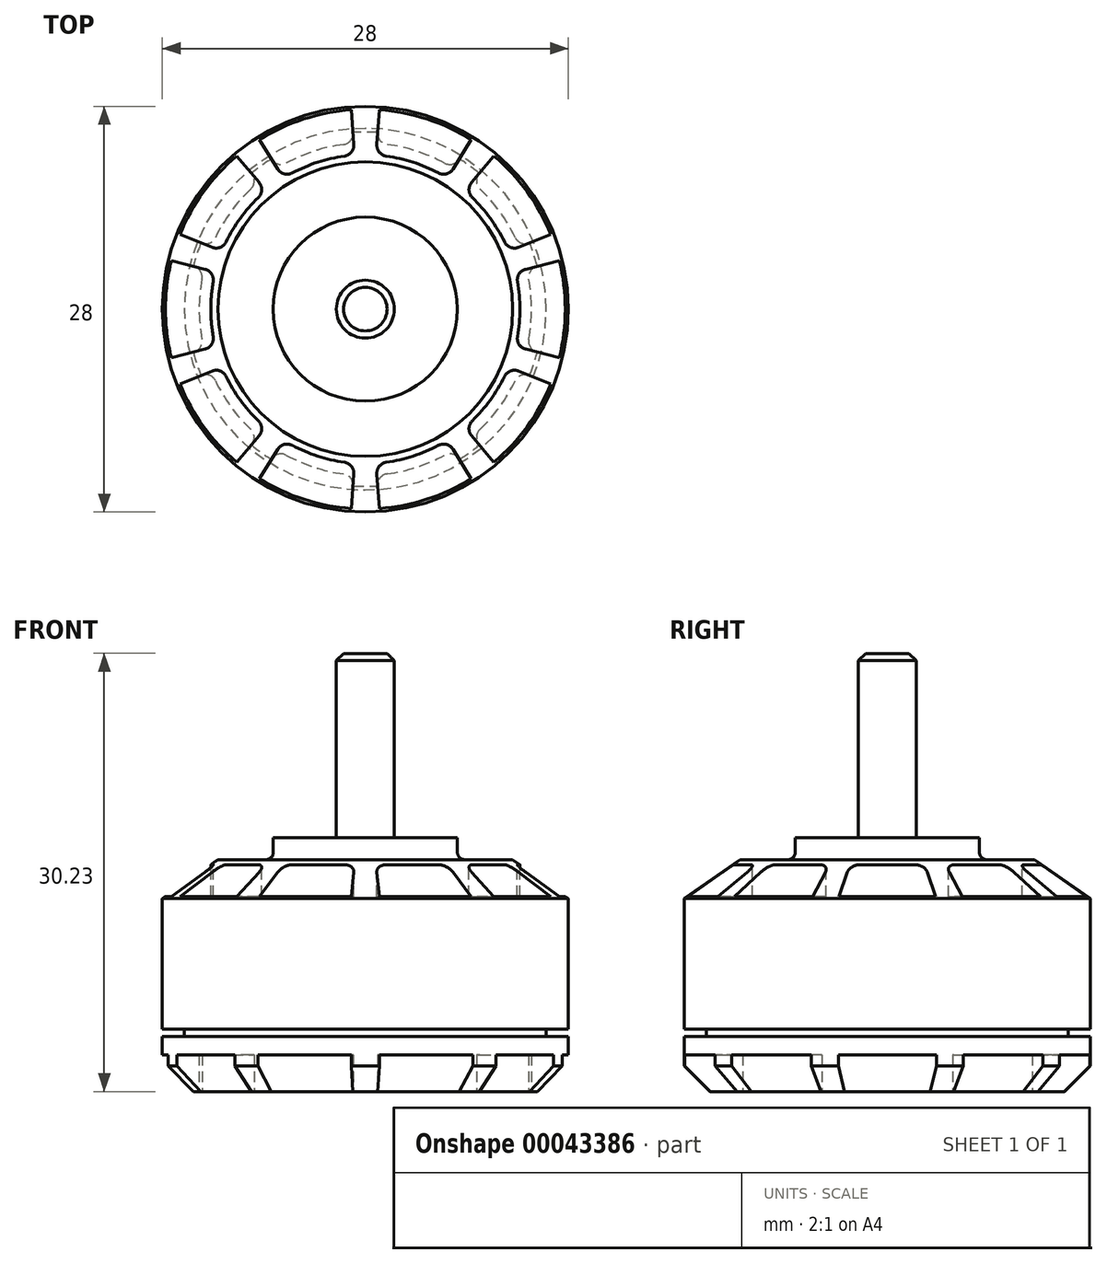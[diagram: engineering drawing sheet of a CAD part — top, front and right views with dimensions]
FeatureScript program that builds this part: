
annotation { "Feature Type Name" : "Feature", "Feature Type Description" : "" }
export const myFeature = defineFeature(function(context is Context, id is Id, definition is map)
    precondition{}
    {
        {
            var Q0;
            Q0=qCreatedBy(makeId("Front.planeOp"),FACE);
            var sketch = newSketch(context, id + "F0", { "sketchPlane" : qUnion([Q0])});
            skLineSegment(sketch, "E0", {"start": v(0, 0) * mm, "end": v(0, 46.88) * mm, "construction": true});
            skLineSegment(sketch, "E1", {"start": v(0, 0) * mm, "end": v(12.22, 0) * mm});
            skLineSegment(sketch, "E2", {"start": v(12.22, 0) * mm, "end": v(14, 1.78) * mm});
            skLineSegment(sketch, "E3", {"start": v(14, 1.78) * mm, "end": v(14, 3.81) * mm});
            skLineSegment(sketch, "E4", {"start": v(14, 3.81) * mm, "end": v(12.48, 3.81) * mm});
            skLineSegment(sketch, "E5", {"start": v(12.48, 3.81) * mm, "end": v(12.48, 4.31) * mm});
            skLineSegment(sketch, "E6", {"start": v(12.48, 4.3) * mm, "end": v(14, 4.31) * mm});
            skLineSegment(sketch, "E7", {"start": v(14, 4.31) * mm, "end": v(14, 13.31) * mm});
            skLineSegment(sketch, "E8", {"start": v(14, 13.31) * mm, "end": v(10.16, 16) * mm});
            skLineSegment(sketch, "E9", {"start": v(10.16, 16) * mm, "end": v(6.35, 16) * mm});
            skLineSegment(sketch, "E10", {"start": v(6.35, 16) * mm, "end": v(6.35, 17.53) * mm});
            skLineSegment(sketch, "E11", {"start": v(6.35, 17.53) * mm, "end": v(2, 17.53) * mm});
            skLineSegment(sketch, "E12", {"start": v(2, 17.53) * mm, "end": v(2, 30.23) * mm});
            skLineSegment(sketch, "E13", {"start": v(2, 30.23) * mm, "end": v(0, 30.23) * mm});
            skLineSegment(sketch, "E14", {"start": v(0, 30.23) * mm, "end": v(0, 0) * mm});
            skSolve(sketch);
        }
        {
            var Q0;
            Q0 = qSketchRegion(id + "F0", true);
            var Q1;
            Q1=sQuery(id+"F0.wireOp",EDGE,"E0");
            revolve(context, id + "F1", {"entities" : qUnion([Q0]), "axis" : qUnion([Q1]), "revolveType" : RevolveType.FULL});
        }
        {
            var Q0;
            Q0=makeQuery(id+"F1.opRevolve","SWEPT_EDGE",EDGE,{"disambiguationData":[OSD([sQuery(id+"F0.wireOp",EDGE,"E12"),sQuery(id+"F0.wireOp",EDGE,"E13")])]});
            chamfer(context, id + "F2", {"entities" : qUnion([Q0]), "width" : .5 * mm, "tangentPropagation" : true});
        }
        {
            var Q0;
            Q0=makeQuery(id+"F1.opRevolve","SWEPT_EDGE",EDGE,{"disambiguationData":[OSD([sQuery(id+"F0.wireOp",EDGE,"E9"),sQuery(id+"F0.wireOp",EDGE,"E10")])]});
            fillet(context, id + "F3", {"entities" : qUnion([Q0]), "radius" : .5 * mm, "tangentPropagation" : true, "allowEdgeOverflow" : false});
        }
        {
            var Q0;
            Q0=makeQuery(id+"F1.opRevolve","SWEPT_FACE",FACE,{"disambiguationData":[OSD([sQuery(id+"F0.wireOp",EDGE,"E9")])]});
            var sketch = newSketch(context, id + "F4", { "sketchPlane" : qUnion([Q0])});
            skArc(sketch, "E15.0", {"start": v(10.5, 1.88) * mm, "mid": v(10.62, 0.95) * mm, "end": v(10.66, 0) * mm});
            skLineSegment(sketch, "E16", {"start": v(11.06, 2.76) * mm, "end": v(13.58, 3.39) * mm});
            skLineSegment(sketch, "E17", {"start": v(0, 0) * mm, "end": v(17.06, 0) * mm, "construction": true});
            skPoint(sketch, "E18.visualSharp", {"position": v(10.34, 2.58) * mm});
            skArc(sketch, "E18.filletArc", {"start": v(11.06, 2.76) * mm, "mid": v(10.6, 2.43) * mm, "end": v(10.5, 1.88) * mm});
            skArc(sketch, "E19.MirrorCS", {"start": v(10.5, -1.88) * mm, "mid": v(10.62, -0.95) * mm, "end": v(10.66, 0) * mm});
            skArc(sketch, "E20.MirrorCS", {"start": v(11.06, -2.76) * mm, "mid": v(10.6, -2.43) * mm, "end": v(10.5, -1.88) * mm});
            skLineSegment(sketch, "E21.MirrorCS", {"start": v(11.06, -2.76) * mm, "end": v(13.58, -3.39) * mm});
            skArc(sketch, "E22.1", {"start": v(13.58, -3.39) * mm, "mid": v(14, 0) * mm, "end": v(13.58, 3.39) * mm});
            skLineSegment(sketch, "E23.1.0", {"start": v(7.33, 8.73) * mm, "end": v(9, 10.72) * mm});
            skArc(sketch, "E23.1.1", {"start": v(7.33, 8.73) * mm, "mid": v(7.15, 8.2) * mm, "end": v(7.38, 7.7) * mm});
            skArc(sketch, "E23.1.2", {"start": v(9.6, 4.64) * mm, "mid": v(9.15, 5.48) * mm, "end": v(8.62, 6.27) * mm});
            skArc(sketch, "E23.1.3", {"start": v(10.57, 4.27) * mm, "mid": v(10, 4.26) * mm, "end": v(9.6, 4.64) * mm});
            skLineSegment(sketch, "E23.1.4", {"start": v(10.57, 4.27) * mm, "end": v(12.98, 5.24) * mm});
            skArc(sketch, "E23.1.5", {"start": v(12.98, 5.24) * mm, "mid": v(11.33, 8.23) * mm, "end": v(9, 10.72) * mm});
            skArc(sketch, "E23.1.6", {"start": v(7.38, 7.7) * mm, "mid": v(8.03, 7) * mm, "end": v(8.62, 6.27) * mm});
            skPoint(sketch, "E23.1.7", {"position": v(6.85, 8.17) * mm});
            skLineSegment(sketch, "E23.2.0", {"start": v(0.8, 11.37) * mm, "end": v(0.98, 13.97) * mm});
            skArc(sketch, "E23.2.1", {"start": v(0.8, 11.37) * mm, "mid": v(0.96, 10.84) * mm, "end": v(1.45, 10.56) * mm});
            skArc(sketch, "E23.2.2", {"start": v(5.03, 9.4) * mm, "mid": v(4.18, 9.8) * mm, "end": v(3.3, 10.14) * mm});
            skArc(sketch, "E23.2.3", {"start": v(6.04, 9.66) * mm, "mid": v(5.59, 9.33) * mm, "end": v(5.03, 9.4) * mm});
            skLineSegment(sketch, "E23.2.4", {"start": v(6.04, 9.66) * mm, "end": v(7.42, 11.87) * mm});
            skArc(sketch, "E23.2.5", {"start": v(7.42, 11.87) * mm, "mid": v(4.33, 13.31) * mm, "end": v(0.98, 13.97) * mm});
            skArc(sketch, "E23.2.6", {"start": v(1.45, 10.56) * mm, "mid": v(2.38, 10.4) * mm, "end": v(3.3, 10.14) * mm});
            skPoint(sketch, "E23.2.7", {"position": v(0.74, 10.63) * mm});
            skLineSegment(sketch, "E23.3.0", {"start": v(-6.04, 9.66) * mm, "end": v(-7.42, 11.87) * mm});
            skArc(sketch, "E23.3.1", {"start": v(-6.04, 9.66) * mm, "mid": v(-5.59, 9.33) * mm, "end": v(-5.03, 9.4) * mm});
            skArc(sketch, "E23.3.2", {"start": v(-1.45, 10.56) * mm, "mid": v(-2.38, 10.4) * mm, "end": v(-3.3, 10.14) * mm});
            skArc(sketch, "E23.3.3", {"start": v(-0.8, 11.37) * mm, "mid": v(-0.96, 10.84) * mm, "end": v(-1.45, 10.56) * mm});
            skLineSegment(sketch, "E23.3.4", {"start": v(-0.8, 11.37) * mm, "end": v(-0.98, 13.97) * mm});
            skArc(sketch, "E23.3.5", {"start": v(-0.98, 13.97) * mm, "mid": v(-4.33, 13.31) * mm, "end": v(-7.42, 11.87) * mm});
            skArc(sketch, "E23.3.6", {"start": v(-5.03, 9.4) * mm, "mid": v(-4.18, 9.8) * mm, "end": v(-3.3, 10.14) * mm});
            skPoint(sketch, "E23.3.7", {"position": v(-5.65, 9.04) * mm});
            skLineSegment(sketch, "E23.4.0", {"start": v(-10.57, 4.27) * mm, "end": v(-12.98, 5.24) * mm});
            skArc(sketch, "E23.4.1", {"start": v(-10.57, 4.27) * mm, "mid": v(-10, 4.26) * mm, "end": v(-9.6, 4.64) * mm});
            skArc(sketch, "E23.4.2", {"start": v(-7.38, 7.7) * mm, "mid": v(-8.03, 7) * mm, "end": v(-8.62, 6.27) * mm});
            skArc(sketch, "E23.4.3", {"start": v(-7.33, 8.73) * mm, "mid": v(-7.15, 8.2) * mm, "end": v(-7.38, 7.7) * mm});
            skLineSegment(sketch, "E23.4.4", {"start": v(-7.33, 8.73) * mm, "end": v(-9, 10.72) * mm});
            skArc(sketch, "E23.4.5", {"start": v(-9, 10.72) * mm, "mid": v(-11.33, 8.23) * mm, "end": v(-12.98, 5.24) * mm});
            skArc(sketch, "E23.4.6", {"start": v(-9.6, 4.64) * mm, "mid": v(-9.15, 5.48) * mm, "end": v(-8.62, 6.27) * mm});
            skPoint(sketch, "E23.4.7", {"position": v(-9.88, 4) * mm});
            skLineSegment(sketch, "E23.5.0", {"start": v(-11.06, -2.76) * mm, "end": v(-13.58, -3.39) * mm});
            skArc(sketch, "E23.5.1", {"start": v(-11.06, -2.76) * mm, "mid": v(-10.6, -2.43) * mm, "end": v(-10.5, -1.88) * mm});
            skArc(sketch, "E23.5.2", {"start": v(-10.5, 1.88) * mm, "mid": v(-10.62, 0.95) * mm, "end": v(-10.66, 0) * mm});
            skArc(sketch, "E23.5.3", {"start": v(-11.06, 2.76) * mm, "mid": v(-10.6, 2.43) * mm, "end": v(-10.5, 1.88) * mm});
            skLineSegment(sketch, "E23.5.4", {"start": v(-11.06, 2.76) * mm, "end": v(-13.58, 3.39) * mm});
            skArc(sketch, "E23.5.5", {"start": v(-13.58, 3.39) * mm, "mid": v(-14, 0) * mm, "end": v(-13.58, -3.39) * mm});
            skArc(sketch, "E23.5.6", {"start": v(-10.5, -1.88) * mm, "mid": v(-10.62, -0.95) * mm, "end": v(-10.66, 0) * mm});
            skPoint(sketch, "E23.5.7", {"position": v(-10.34, -2.58) * mm});
            skLineSegment(sketch, "E23.6.0", {"start": v(-7.33, -8.73) * mm, "end": v(-9, -10.72) * mm});
            skArc(sketch, "E23.6.1", {"start": v(-7.33, -8.73) * mm, "mid": v(-7.15, -8.2) * mm, "end": v(-7.38, -7.7) * mm});
            skArc(sketch, "E23.6.2", {"start": v(-9.6, -4.64) * mm, "mid": v(-9.15, -5.48) * mm, "end": v(-8.62, -6.27) * mm});
            skArc(sketch, "E23.6.3", {"start": v(-10.57, -4.27) * mm, "mid": v(-10, -4.26) * mm, "end": v(-9.6, -4.64) * mm});
            skLineSegment(sketch, "E23.6.4", {"start": v(-10.57, -4.27) * mm, "end": v(-12.98, -5.24) * mm});
            skArc(sketch, "E23.6.5", {"start": v(-12.98, -5.24) * mm, "mid": v(-11.33, -8.23) * mm, "end": v(-9, -10.72) * mm});
            skArc(sketch, "E23.6.6", {"start": v(-7.38, -7.7) * mm, "mid": v(-8.03, -7) * mm, "end": v(-8.62, -6.27) * mm});
            skPoint(sketch, "E23.6.7", {"position": v(-6.85, -8.17) * mm});
            skLineSegment(sketch, "E23.7.0", {"start": v(-0.8, -11.37) * mm, "end": v(-0.98, -13.97) * mm});
            skArc(sketch, "E23.7.1", {"start": v(-0.8, -11.37) * mm, "mid": v(-0.96, -10.84) * mm, "end": v(-1.45, -10.56) * mm});
            skArc(sketch, "E23.7.2", {"start": v(-5.03, -9.4) * mm, "mid": v(-4.18, -9.8) * mm, "end": v(-3.3, -10.14) * mm});
            skArc(sketch, "E23.7.3", {"start": v(-6.04, -9.66) * mm, "mid": v(-5.59, -9.33) * mm, "end": v(-5.03, -9.4) * mm});
            skLineSegment(sketch, "E23.7.4", {"start": v(-6.04, -9.66) * mm, "end": v(-7.42, -11.87) * mm});
            skArc(sketch, "E23.7.5", {"start": v(-7.42, -11.87) * mm, "mid": v(-4.33, -13.31) * mm, "end": v(-0.98, -13.97) * mm});
            skArc(sketch, "E23.7.6", {"start": v(-1.45, -10.56) * mm, "mid": v(-2.38, -10.4) * mm, "end": v(-3.3, -10.14) * mm});
            skPoint(sketch, "E23.7.7", {"position": v(-0.74, -10.63) * mm});
            skLineSegment(sketch, "E23.8.0", {"start": v(6.04, -9.66) * mm, "end": v(7.42, -11.87) * mm});
            skArc(sketch, "E23.8.1", {"start": v(6.04, -9.66) * mm, "mid": v(5.59, -9.33) * mm, "end": v(5.03, -9.4) * mm});
            skArc(sketch, "E23.8.2", {"start": v(1.45, -10.56) * mm, "mid": v(2.38, -10.4) * mm, "end": v(3.3, -10.14) * mm});
            skArc(sketch, "E23.8.3", {"start": v(0.8, -11.37) * mm, "mid": v(0.96, -10.84) * mm, "end": v(1.45, -10.56) * mm});
            skLineSegment(sketch, "E23.8.4", {"start": v(0.8, -11.37) * mm, "end": v(0.98, -13.97) * mm});
            skArc(sketch, "E23.8.5", {"start": v(0.98, -13.97) * mm, "mid": v(4.33, -13.31) * mm, "end": v(7.42, -11.87) * mm});
            skArc(sketch, "E23.8.6", {"start": v(5.03, -9.4) * mm, "mid": v(4.18, -9.8) * mm, "end": v(3.3, -10.14) * mm});
            skPoint(sketch, "E23.8.7", {"position": v(5.65, -9.04) * mm});
            skLineSegment(sketch, "E23.9.0", {"start": v(10.57, -4.27) * mm, "end": v(12.98, -5.24) * mm});
            skArc(sketch, "E23.9.1", {"start": v(10.57, -4.27) * mm, "mid": v(10, -4.26) * mm, "end": v(9.6, -4.64) * mm});
            skArc(sketch, "E23.9.2", {"start": v(7.38, -7.7) * mm, "mid": v(8.03, -7) * mm, "end": v(8.62, -6.27) * mm});
            skArc(sketch, "E23.9.3", {"start": v(7.33, -8.73) * mm, "mid": v(7.15, -8.2) * mm, "end": v(7.38, -7.7) * mm});
            skLineSegment(sketch, "E23.9.4", {"start": v(7.33, -8.73) * mm, "end": v(9, -10.72) * mm});
            skArc(sketch, "E23.9.5", {"start": v(9, -10.72) * mm, "mid": v(11.33, -8.23) * mm, "end": v(12.98, -5.24) * mm});
            skArc(sketch, "E23.9.6", {"start": v(9.6, -4.64) * mm, "mid": v(9.15, -5.48) * mm, "end": v(8.62, -6.27) * mm});
            skPoint(sketch, "E23.9.7", {"position": v(9.88, -4) * mm});
            skSolve(sketch);
        }
        {
            var Q0;
            Q0 = qSketchRegion(id + "F4", true);
            extrude(context, id + "F5", {"entities" : qUnion([Q0]), "operationType" : NewBodyOperationType.REMOVE, "oppositeDirection" : true, "depth" : 2.54 * mm});
        }
        {
            var Q0;
            Q0=makeQuery(id+"F1.opRevolve","SWEPT_FACE",FACE,{"disambiguationData":[OSD([sQuery(id+"F0.wireOp",EDGE,"E1")])]});
            var sketch = newSketch(context, id + "F6", { "sketchPlane" : qUnion([Q0])});
            skLineSegment(sketch, "E24.0", {"start": v(11.84, 2.95) * mm, "end": v(13.58, 3.39) * mm});
            skLineSegment(sketch, "E24.1", {"start": v(11.84, -2.95) * mm, "end": v(13.58, -3.39) * mm});
            skArc(sketch, "E25.0", {"start": v(11.27, -2.07) * mm, "mid": v(11.46, 0) * mm, "end": v(11.27, 2.07) * mm});
            skPoint(sketch, "E26.newPointB", {"position": v(11.06, 2.76) * mm});
            skArc(sketch, "E26.filletArc", {"start": v(11.84, 2.95) * mm, "mid": v(11.38, 2.62) * mm, "end": v(11.27, 2.07) * mm});
            skPoint(sketch, "E27.newPointB", {"position": v(11.06, -2.76) * mm});
            skArc(sketch, "E27.filletArc", {"start": v(11.27, -2.07) * mm, "mid": v(11.38, -2.62) * mm, "end": v(11.84, -2.95) * mm});
            skArc(sketch, "E28.0", {"start": v(13.58, 3.39) * mm, "mid": v(14, 0) * mm, "end": v(13.58, -3.39) * mm});
            skArc(sketch, "E29.1.0", {"start": v(9, 10.72) * mm, "mid": v(11.33, 8.23) * mm, "end": v(12.98, 5.24) * mm});
            skPoint(sketch, "E29.1.1", {"position": v(7.33, 8.73) * mm});
            skArc(sketch, "E29.1.2", {"start": v(10.34, 4.95) * mm, "mid": v(9.27, 6.74) * mm, "end": v(7.9, 8.3) * mm});
            skPoint(sketch, "E29.1.3", {"position": v(10.57, 4.27) * mm});
            skArc(sketch, "E29.1.4", {"start": v(7.84, 9.34) * mm, "mid": v(7.66, 8.81) * mm, "end": v(7.9, 8.3) * mm});
            skLineSegment(sketch, "E29.1.5", {"start": v(7.84, 9.34) * mm, "end": v(9, 10.72) * mm});
            skArc(sketch, "E29.1.6", {"start": v(10.34, 4.95) * mm, "mid": v(10.75, 4.57) * mm, "end": v(11.3, 4.57) * mm});
            skLineSegment(sketch, "E29.1.7", {"start": v(11.3, 4.57) * mm, "end": v(12.98, 5.24) * mm});
            skArc(sketch, "E29.2.0", {"start": v(0.98, 13.97) * mm, "mid": v(4.33, 13.31) * mm, "end": v(7.42, 11.87) * mm});
            skPoint(sketch, "E29.2.1", {"position": v(0.8, 11.37) * mm});
            skArc(sketch, "E29.2.2", {"start": v(5.46, 10.08) * mm, "mid": v(3.54, 10.9) * mm, "end": v(1.51, 11.36) * mm});
            skPoint(sketch, "E29.2.3", {"position": v(6.04, 9.66) * mm});
            skArc(sketch, "E29.2.4", {"start": v(0.85, 12.17) * mm, "mid": v(1.02, 11.63) * mm, "end": v(1.51, 11.36) * mm});
            skLineSegment(sketch, "E29.2.5", {"start": v(0.85, 12.17) * mm, "end": v(0.98, 13.97) * mm});
            skArc(sketch, "E29.2.6", {"start": v(5.46, 10.08) * mm, "mid": v(6.01, 10.01) * mm, "end": v(6.46, 10.34) * mm});
            skLineSegment(sketch, "E29.2.7", {"start": v(6.46, 10.34) * mm, "end": v(7.42, 11.87) * mm});
            skArc(sketch, "E29.3.0", {"start": v(-7.42, 11.87) * mm, "mid": v(-4.33, 13.31) * mm, "end": v(-0.98, 13.97) * mm});
            skPoint(sketch, "E29.3.1", {"position": v(-6.04, 9.66) * mm});
            skArc(sketch, "E29.3.2", {"start": v(-1.51, 11.36) * mm, "mid": v(-3.54, 10.9) * mm, "end": v(-5.46, 10.08) * mm});
            skPoint(sketch, "E29.3.3", {"position": v(-0.8, 11.37) * mm});
            skArc(sketch, "E29.3.4", {"start": v(-6.46, 10.34) * mm, "mid": v(-6.01, 10.01) * mm, "end": v(-5.46, 10.08) * mm});
            skLineSegment(sketch, "E29.3.5", {"start": v(-6.46, 10.34) * mm, "end": v(-7.42, 11.87) * mm});
            skArc(sketch, "E29.3.6", {"start": v(-1.51, 11.36) * mm, "mid": v(-1.02, 11.63) * mm, "end": v(-0.85, 12.17) * mm});
            skLineSegment(sketch, "E29.3.7", {"start": v(-0.85, 12.17) * mm, "end": v(-0.98, 13.97) * mm});
            skArc(sketch, "E29.4.0", {"start": v(-12.98, 5.24) * mm, "mid": v(-11.33, 8.23) * mm, "end": v(-9, 10.72) * mm});
            skPoint(sketch, "E29.4.1", {"position": v(-10.57, 4.27) * mm});
            skArc(sketch, "E29.4.2", {"start": v(-7.9, 8.3) * mm, "mid": v(-9.27, 6.74) * mm, "end": v(-10.34, 4.95) * mm});
            skPoint(sketch, "E29.4.3", {"position": v(-7.33, 8.73) * mm});
            skArc(sketch, "E29.4.4", {"start": v(-11.3, 4.57) * mm, "mid": v(-10.75, 4.57) * mm, "end": v(-10.34, 4.95) * mm});
            skLineSegment(sketch, "E29.4.5", {"start": v(-11.3, 4.57) * mm, "end": v(-12.98, 5.24) * mm});
            skArc(sketch, "E29.4.6", {"start": v(-7.9, 8.3) * mm, "mid": v(-7.66, 8.81) * mm, "end": v(-7.84, 9.34) * mm});
            skLineSegment(sketch, "E29.4.7", {"start": v(-7.84, 9.34) * mm, "end": v(-9, 10.72) * mm});
            skArc(sketch, "E29.5.0", {"start": v(-13.58, -3.39) * mm, "mid": v(-14, 0) * mm, "end": v(-13.58, 3.39) * mm});
            skPoint(sketch, "E29.5.1", {"position": v(-11.06, -2.76) * mm});
            skArc(sketch, "E29.5.2", {"start": v(-11.27, 2.07) * mm, "mid": v(-11.46, 0) * mm, "end": v(-11.27, -2.07) * mm});
            skPoint(sketch, "E29.5.3", {"position": v(-11.06, 2.76) * mm});
            skArc(sketch, "E29.5.4", {"start": v(-11.84, -2.95) * mm, "mid": v(-11.38, -2.62) * mm, "end": v(-11.27, -2.07) * mm});
            skLineSegment(sketch, "E29.5.5", {"start": v(-11.84, -2.95) * mm, "end": v(-13.58, -3.39) * mm});
            skArc(sketch, "E29.5.6", {"start": v(-11.27, 2.07) * mm, "mid": v(-11.38, 2.62) * mm, "end": v(-11.84, 2.95) * mm});
            skLineSegment(sketch, "E29.5.7", {"start": v(-11.84, 2.95) * mm, "end": v(-13.58, 3.39) * mm});
            skArc(sketch, "E29.6.0", {"start": v(-9, -10.72) * mm, "mid": v(-11.33, -8.23) * mm, "end": v(-12.98, -5.24) * mm});
            skPoint(sketch, "E29.6.1", {"position": v(-7.33, -8.73) * mm});
            skArc(sketch, "E29.6.2", {"start": v(-10.34, -4.95) * mm, "mid": v(-9.27, -6.74) * mm, "end": v(-7.9, -8.3) * mm});
            skPoint(sketch, "E29.6.3", {"position": v(-10.57, -4.27) * mm});
            skArc(sketch, "E29.6.4", {"start": v(-7.84, -9.34) * mm, "mid": v(-7.66, -8.81) * mm, "end": v(-7.9, -8.3) * mm});
            skLineSegment(sketch, "E29.6.5", {"start": v(-7.84, -9.34) * mm, "end": v(-9, -10.72) * mm});
            skArc(sketch, "E29.6.6", {"start": v(-10.34, -4.95) * mm, "mid": v(-10.75, -4.57) * mm, "end": v(-11.3, -4.57) * mm});
            skLineSegment(sketch, "E29.6.7", {"start": v(-11.3, -4.57) * mm, "end": v(-12.98, -5.24) * mm});
            skArc(sketch, "E29.7.0", {"start": v(-0.98, -13.97) * mm, "mid": v(-4.33, -13.31) * mm, "end": v(-7.42, -11.87) * mm});
            skPoint(sketch, "E29.7.1", {"position": v(-0.8, -11.37) * mm});
            skArc(sketch, "E29.7.2", {"start": v(-5.46, -10.08) * mm, "mid": v(-3.54, -10.9) * mm, "end": v(-1.51, -11.36) * mm});
            skPoint(sketch, "E29.7.3", {"position": v(-6.04, -9.66) * mm});
            skArc(sketch, "E29.7.4", {"start": v(-0.85, -12.17) * mm, "mid": v(-1.02, -11.63) * mm, "end": v(-1.51, -11.36) * mm});
            skLineSegment(sketch, "E29.7.5", {"start": v(-0.85, -12.17) * mm, "end": v(-0.98, -13.97) * mm});
            skArc(sketch, "E29.7.6", {"start": v(-5.46, -10.08) * mm, "mid": v(-6.01, -10.01) * mm, "end": v(-6.46, -10.34) * mm});
            skLineSegment(sketch, "E29.7.7", {"start": v(-6.46, -10.34) * mm, "end": v(-7.42, -11.87) * mm});
            skArc(sketch, "E29.8.0", {"start": v(7.42, -11.87) * mm, "mid": v(4.33, -13.31) * mm, "end": v(0.98, -13.97) * mm});
            skPoint(sketch, "E29.8.1", {"position": v(6.04, -9.66) * mm});
            skArc(sketch, "E29.8.2", {"start": v(1.51, -11.36) * mm, "mid": v(3.54, -10.9) * mm, "end": v(5.46, -10.08) * mm});
            skPoint(sketch, "E29.8.3", {"position": v(0.8, -11.37) * mm});
            skArc(sketch, "E29.8.4", {"start": v(6.46, -10.34) * mm, "mid": v(6.01, -10.01) * mm, "end": v(5.46, -10.08) * mm});
            skLineSegment(sketch, "E29.8.5", {"start": v(6.46, -10.34) * mm, "end": v(7.42, -11.87) * mm});
            skArc(sketch, "E29.8.6", {"start": v(1.51, -11.36) * mm, "mid": v(1.02, -11.63) * mm, "end": v(0.85, -12.17) * mm});
            skLineSegment(sketch, "E29.8.7", {"start": v(0.85, -12.17) * mm, "end": v(0.98, -13.97) * mm});
            skArc(sketch, "E29.9.0", {"start": v(12.98, -5.24) * mm, "mid": v(11.33, -8.23) * mm, "end": v(9, -10.72) * mm});
            skPoint(sketch, "E29.9.1", {"position": v(10.57, -4.27) * mm});
            skArc(sketch, "E29.9.2", {"start": v(7.9, -8.3) * mm, "mid": v(9.27, -6.74) * mm, "end": v(10.34, -4.95) * mm});
            skPoint(sketch, "E29.9.3", {"position": v(7.33, -8.73) * mm});
            skArc(sketch, "E29.9.4", {"start": v(11.3, -4.57) * mm, "mid": v(10.75, -4.57) * mm, "end": v(10.34, -4.95) * mm});
            skLineSegment(sketch, "E29.9.5", {"start": v(11.3, -4.57) * mm, "end": v(12.98, -5.24) * mm});
            skArc(sketch, "E29.9.6", {"start": v(7.9, -8.3) * mm, "mid": v(7.66, -8.81) * mm, "end": v(7.84, -9.34) * mm});
            skLineSegment(sketch, "E29.9.7", {"start": v(7.84, -9.34) * mm, "end": v(9, -10.72) * mm});
            skSolve(sketch);
        }
        {
            var Q0;
            Q0 = qSketchRegion(id + "F6", true);
            extrude(context, id + "F7", {"entities" : qUnion([Q0]), "operationType" : NewBodyOperationType.REMOVE, "oppositeDirection" : true, "depth" : 2.54 * mm});
        }
    });
